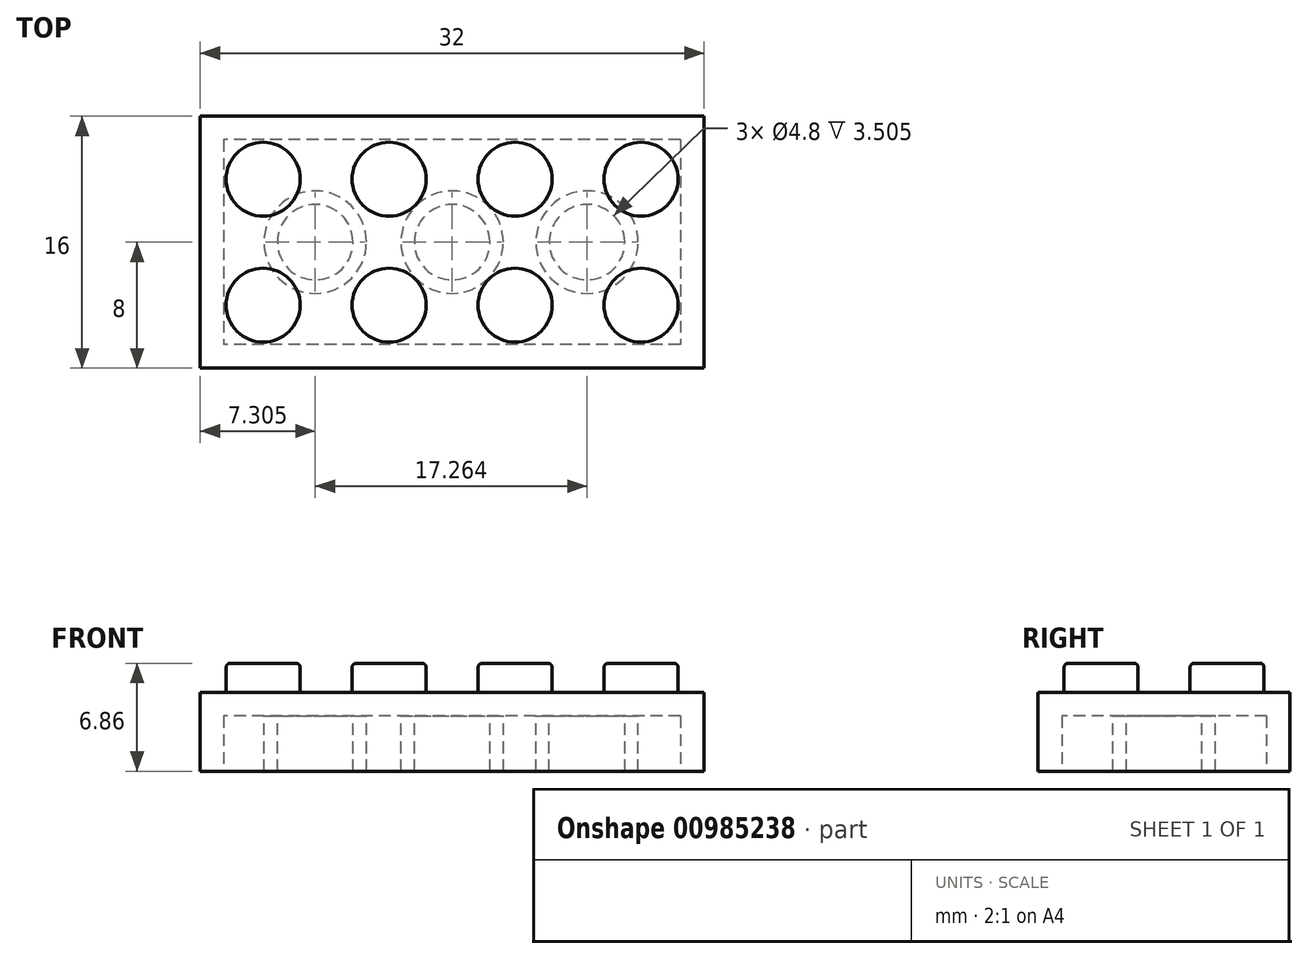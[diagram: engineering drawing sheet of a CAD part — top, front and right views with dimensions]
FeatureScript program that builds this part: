
annotation { "Feature Type Name" : "Feature", "Feature Type Description" : "" }
export const myFeature = defineFeature(function(context is Context, id is Id, definition is map)
    precondition{}
    {
        {
            var Q0;
            Q0=qCreatedBy(makeId("Top.planeOp"),FACE);
            var sketch = newSketch(context, id + "F0", { "sketchPlane" : qUnion([Q0])});
            skLineSegment(sketch, "E0.bottom", {"start": v(16, 8) * mm, "end": v(-16, 8) * mm});
            skLineSegment(sketch, "E0.top", {"start": v(16, -8) * mm, "end": v(-16, -8) * mm});
            skLineSegment(sketch, "E0.left", {"start": v(16, 8) * mm, "end": v(16, -8) * mm});
            skLineSegment(sketch, "E0.right", {"start": v(-16, 8) * mm, "end": v(-16, -8) * mm});
            skPoint(sketch, "E0.middle", {"position": v(0, 0) * mm});
            skSolve(sketch);
        }
        {
            var Q0;
            Q0=makeQuery(id+"F0.imprint","IMPRINT",FACE,{"disambiguationData":[TD([[makeQuery(id+"F0.imprint","IMPRINT",EDGE,{"derivedFrom":sQuery(id+"F0.wireOp",EDGE,"E0.bottom")}),1.0]])]});
            extrude(context, id + "F1", {"entities" : qUnion([Q0]), "depth" : 5 * mm, "offsetDistance" : 25.4 * mm});
        }
        {
            var Q0;
            Q0=makeQuery(id+"F1.opExtrude","CAP_FACE",FACE,{"disambiguationData":[OSD([sQuery(id+"F0.wireOp",EDGE,"E0.bottom"),sQuery(id+"F0.wireOp",EDGE,"E0.top"),sQuery(id+"F0.wireOp",EDGE,"E0.left"),sQuery(id+"F0.wireOp",EDGE,"E0.right")])],"isStart":true});
            var sketch = newSketch(context, id + "F2", { "sketchPlane" : qUnion([Q0])});
            skLineSegment(sketch, "E1.0", {"start": v(14.5, 6.5) * mm, "end": v(-14.5, 6.5) * mm});
            skLineSegment(sketch, "E1.1", {"start": v(14.5, -6.5) * mm, "end": v(14.5, 6.5) * mm});
            skLineSegment(sketch, "E1.2", {"start": v(14.5, -6.5) * mm, "end": v(-14.5, -6.5) * mm});
            skLineSegment(sketch, "E1.3", {"start": v(-14.5, -6.5) * mm, "end": v(-14.5, 6.5) * mm});
            skSolve(sketch);
        }
        {
            var Q0;
            Q0=makeQuery(id+"F2.imprint","IMPRINT",FACE,{"disambiguationData":[TD([[makeQuery(id+"F2.imprint","IMPRINT",EDGE,{"derivedFrom":sQuery(id+"F2.wireOp",EDGE,"E1.0")}),1.0]])]});
            extrude(context, id + "F3", {"entities" : qUnion([Q0]), "operationType" : NewBodyOperationType.REMOVE, "oppositeDirection" : true, "depth" : 3.5 * mm, "offsetDistance" : 25.4 * mm});
        }
        {
            var Q0;
            Q0=makeQuery(id+"F3.boolean.opBoolean","COPY",FACE,{"derivedFrom":makeQuery(id+"F3.opExtrude","CAP_FACE",FACE,{"disambiguationData":[OSD([sQuery(id+"F2.wireOp",EDGE,"E1.0"),sQuery(id+"F2.wireOp",EDGE,"E1.1"),sQuery(id+"F2.wireOp",EDGE,"E1.2"),sQuery(id+"F2.wireOp",EDGE,"E1.3")])],"isStart":false})});
            var sketch = newSketch(context, id + "F4", { "sketchPlane" : qUnion([Q0])});
            skCircle(sketch, "E2", {"center": v(0, 0) * mm, "radius": 3.25 * mm});
            skCircle(sketch, "E3", {"center": v(0, 0) * mm, "radius": 2.4 * mm});
            skCircle(sketch, "E4", {"center": v(8.57, 0) * mm, "radius": 3.25 * mm});
            skCircle(sketch, "E5", {"center": v(8.57, 0) * mm, "radius": 2.4 * mm});
            skCircle(sketch, "E6", {"center": v(-8.7, 0) * mm, "radius": 3.25 * mm});
            skCircle(sketch, "E7", {"center": v(-8.7, 0) * mm, "radius": 2.4 * mm});
            skSolve(sketch);
        }
        {
            var Q0;
            Q0 = qSketchRegion(id + "F4", true);
            extrude(context, id + "F5", {"entities" : qUnion([Q0]), "operationType" : NewBodyOperationType.ADD, "depth" : 3.5 * mm, "offsetDistance" : 25.4 * mm});
        }
        {
            var Q0;
            Q0=makeQuery(id+"F1.opExtrude","CAP_FACE",FACE,{"disambiguationData":[OSD([sQuery(id+"F0.wireOp",EDGE,"E0.bottom"),sQuery(id+"F0.wireOp",EDGE,"E0.top"),sQuery(id+"F0.wireOp",EDGE,"E0.left"),sQuery(id+"F0.wireOp",EDGE,"E0.right")])],"isStart":false});
            var sketch = newSketch(context, id + "F6", { "sketchPlane" : qUnion([Q0])});
            skLineSegment(sketch, "E8", {"start": v(-16, 4) * mm, "end": v(16, 4) * mm, "construction": true});
            skLineSegment(sketch, "E9", {"start": v(-16, -4) * mm, "end": v(16, -4) * mm, "construction": true});
            skCircle(sketch, "E10", {"center": v(-12, 4) * mm, "radius": 2.35 * mm});
            skCircle(sketch, "E11", {"center": v(-4, 4) * mm, "radius": 2.35 * mm});
            skCircle(sketch, "E12", {"center": v(4, 4) * mm, "radius": 2.35 * mm});
            skCircle(sketch, "E13", {"center": v(12, 4) * mm, "radius": 2.35 * mm});
            skCircle(sketch, "E14", {"center": v(-12, -4) * mm, "radius": 2.35 * mm});
            skCircle(sketch, "E15", {"center": v(-4, -4) * mm, "radius": 2.35 * mm});
            skCircle(sketch, "E16", {"center": v(4, -4) * mm, "radius": 2.35 * mm});
            skCircle(sketch, "E17", {"center": v(12, -4) * mm, "radius": 2.35 * mm});
            skSolve(sketch);
        }
        {
            var Q0;
            Q0=makeQuery(id+"F6.imprint","IMPRINT",FACE,{"disambiguationData":[TD([[makeQuery(id+"F6.imprint","IMPRINT",EDGE,{"derivedFrom":sQuery(id+"F6.wireOp",EDGE,"E10")}),1.0]])]});
            var Q1;
            Q1=makeQuery(id+"F6.imprint","IMPRINT",FACE,{"disambiguationData":[TD([[makeQuery(id+"F6.imprint","IMPRINT",EDGE,{"derivedFrom":sQuery(id+"F6.wireOp",EDGE,"E11")}),1.0]])]});
            var Q2;
            Q2=makeQuery(id+"F6.imprint","IMPRINT",FACE,{"disambiguationData":[TD([[makeQuery(id+"F6.imprint","IMPRINT",EDGE,{"derivedFrom":sQuery(id+"F6.wireOp",EDGE,"E12")}),1.0]])]});
            var Q3;
            Q3=makeQuery(id+"F6.imprint","IMPRINT",FACE,{"disambiguationData":[TD([[makeQuery(id+"F6.imprint","IMPRINT",EDGE,{"derivedFrom":sQuery(id+"F6.wireOp",EDGE,"E13")}),1.0]])]});
            var Q4;
            Q4=makeQuery(id+"F6.imprint","IMPRINT",FACE,{"disambiguationData":[TD([[makeQuery(id+"F6.imprint","IMPRINT",EDGE,{"derivedFrom":sQuery(id+"F6.wireOp",EDGE,"E14")}),1.0]])]});
            var Q5;
            Q5=makeQuery(id+"F6.imprint","IMPRINT",FACE,{"disambiguationData":[TD([[makeQuery(id+"F6.imprint","IMPRINT",EDGE,{"derivedFrom":sQuery(id+"F6.wireOp",EDGE,"E15")}),1.0]])]});
            var Q6;
            Q6=makeQuery(id+"F6.imprint","IMPRINT",FACE,{"disambiguationData":[TD([[makeQuery(id+"F6.imprint","IMPRINT",EDGE,{"derivedFrom":sQuery(id+"F6.wireOp",EDGE,"E16")}),1.0]])]});
            var Q7;
            Q7=makeQuery(id+"F6.imprint","IMPRINT",FACE,{"disambiguationData":[TD([[makeQuery(id+"F6.imprint","IMPRINT",EDGE,{"derivedFrom":sQuery(id+"F6.wireOp",EDGE,"E17")}),1.0]])]});
            extrude(context, id + "F7", {"entities" : qUnion([Q0, Q1, Q2, Q3, Q4, Q5, Q6, Q7]), "depth" : 1.85 * mm, "offsetDistance" : 25.4 * mm});
        }
        {
            var Q0;
            Q0=makeQuery(id+"F7.opExtrude","CAP_EDGE",EDGE,{"disambiguationData":[OSD([sQuery(id+"F6.wireOp",EDGE,"E14")])],"isStart":false});
            var Q1;
            Q1=makeQuery(id+"F7.opExtrude","CAP_EDGE",EDGE,{"disambiguationData":[OSD([sQuery(id+"F6.wireOp",EDGE,"E10")])],"isStart":false});
            var Q2;
            Q2=makeQuery(id+"F7.opExtrude","CAP_EDGE",EDGE,{"disambiguationData":[OSD([sQuery(id+"F6.wireOp",EDGE,"E15")])],"isStart":false});
            var Q3;
            Q3=makeQuery(id+"F7.opExtrude","CAP_EDGE",EDGE,{"disambiguationData":[OSD([sQuery(id+"F6.wireOp",EDGE,"E11")])],"isStart":false});
            var Q4;
            Q4=makeQuery(id+"F7.opExtrude","CAP_EDGE",EDGE,{"disambiguationData":[OSD([sQuery(id+"F6.wireOp",EDGE,"E16")])],"isStart":false});
            var Q5;
            Q5=makeQuery(id+"F7.opExtrude","CAP_EDGE",EDGE,{"disambiguationData":[OSD([sQuery(id+"F6.wireOp",EDGE,"E12")])],"isStart":false});
            var Q6;
            Q6=makeQuery(id+"F7.opExtrude","CAP_EDGE",EDGE,{"disambiguationData":[OSD([sQuery(id+"F6.wireOp",EDGE,"E13")])],"isStart":false});
            var Q7;
            Q7=makeQuery(id+"F7.opExtrude","CAP_EDGE",EDGE,{"disambiguationData":[OSD([sQuery(id+"F6.wireOp",EDGE,"E17")])],"isStart":false});
            fillet(context, id + "F8", {"entities" : qUnion([Q0, Q1, Q2, Q3, Q4, Q5, Q6, Q7]), "radius" : 0.25 * mm, "tangentPropagation" : true, "allowEdgeOverflow" : false});
        }
    });
